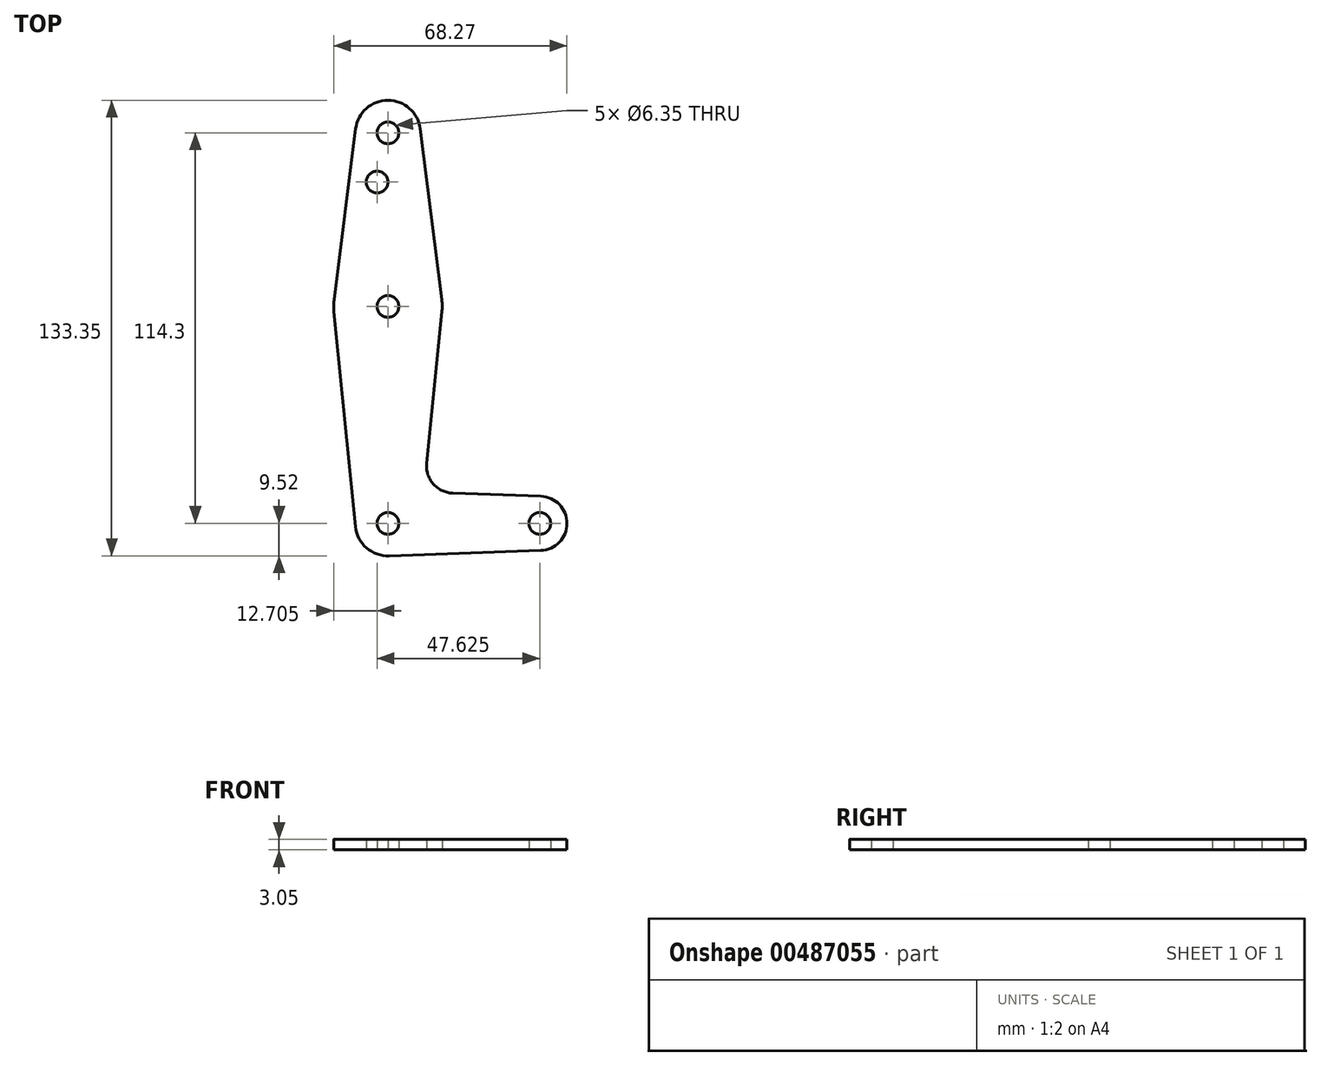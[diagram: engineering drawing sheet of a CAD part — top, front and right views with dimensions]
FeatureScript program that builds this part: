
annotation { "Feature Type Name" : "Feature", "Feature Type Description" : "" }
export const myFeature = defineFeature(function(context is Context, id is Id, definition is map)
    precondition{}
    {
        {
            var Q0;
            Q0=qCreatedBy(makeId("Top.planeOp"),FACE);
            var sketch = newSketch(context, id + "F0", { "sketchPlane" : qUnion([Q0])});
            skLineSegment(sketch, "E0", {"start": v(0, 0) * mm, "end": v(0, 114.3) * mm, "construction": true});
            skLineSegment(sketch, "E1", {"start": v(0, 0) * mm, "end": v(44.45, 0) * mm, "construction": true});
            skCircle(sketch, "E2", {"center": v(0, 0) * mm, "radius": 9.53 * mm});
            skCircle(sketch, "E3", {"center": v(0, 114.3) * mm, "radius": 9.53 * mm});
            skCircle(sketch, "E4", {"center": v(44.45, 0) * mm, "radius": 7.94 * mm});
            skCircle(sketch, "E5", {"center": v(0, 63.5) * mm, "radius": 15.88 * mm});
            skLineSegment(sketch, "E6", {"start": v(9.45, 115.5) * mm, "end": v(15.75, 65.48) * mm});
            skLineSegment(sketch, "E7", {"start": v(-15.8, 61.91) * mm, "end": v(-9.48, -0.95) * mm});
            skLineSegment(sketch, "E8", {"start": v(-9.45, 115.5) * mm, "end": v(-15.75, 65.48) * mm});
            skLineSegment(sketch, "E9", {"start": v(11.3, 17.6) * mm, "end": v(15.8, 61.9) * mm});
            skLineSegment(sketch, "E10", {"start": v(0.34, -9.52) * mm, "end": v(44.73, -7.93) * mm});
            skLineSegment(sketch, "E11", {"start": v(18.93, 8.85) * mm, "end": v(44.73, 7.93) * mm});
            skCircle(sketch, "E12", {"center": v(0, 114.3) * mm, "radius": 3.18 * mm});
            skCircle(sketch, "E13", {"center": v(-3.18, 99.89) * mm, "radius": 3.18 * mm});
            skCircle(sketch, "E14", {"center": v(0, 63.5) * mm, "radius": 3.18 * mm});
            skCircle(sketch, "E15", {"center": v(0, 0) * mm, "radius": 3.18 * mm});
            skCircle(sketch, "E16", {"center": v(44.45, 0) * mm, "radius": 3.18 * mm});
            skArc(sketch, "E17.filletArc", {"start": v(11.3, 17.6) * mm, "mid": v(13.22, 11.57) * mm, "end": v(18.93, 8.85) * mm});
            skSolve(sketch);
        }
        {
            var Q0;
            Q0=makeQuery(id+"F0.imprint","IMPRINT",FACE,{"disambiguationData":[TD([[makeQuery(id+"F0.imprint","IMPRINT",EDGE,{"derivedFrom":sQuery(id+"F0.wireOp",EDGE,"E12")}),-1.0]])]});
            var Q1;
            {var subQ1=sQuery(id+"F0.wireOp",EDGE,"E6");Q1=makeQuery(id+"F0.imprint","IMPRINT",FACE,{"disambiguationData":[TD([[makeQuery(id+"F0.imprint","IMPRINT",EDGE,{"derivedFrom":subQ1}),-1.0]])]});}
            var Q2;
            Q2=makeQuery(id+"F0.imprint","IMPRINT",FACE,{"disambiguationData":[TD([[makeQuery(id+"F0.imprint","IMPRINT",EDGE,{"derivedFrom":sQuery(id+"F0.wireOp",EDGE,"E14")}),-1.0]])]});
            var Q3;
            {var subQ0=sQuery(id+"F0.wireOp",EDGE,"E7");Q3=makeQuery(id+"F0.imprint","IMPRINT",FACE,{"disambiguationData":[TD([[makeQuery(id+"F0.imprint","IMPRINT",EDGE,{"derivedFrom":subQ0}),1.0]])]});}
            var Q4;
            Q4=makeQuery(id+"F0.imprint","IMPRINT",FACE,{"disambiguationData":[TD([[makeQuery(id+"F0.imprint","IMPRINT",EDGE,{"derivedFrom":sQuery(id+"F0.wireOp",EDGE,"E15")}),-1.0]])]});
            var Q5;
            Q5=makeQuery(id+"F0.imprint","IMPRINT",FACE,{"disambiguationData":[TD([[makeQuery(id+"F0.imprint","IMPRINT",EDGE,{"derivedFrom":sQuery(id+"F0.wireOp",EDGE,"E16")}),-1.0]])]});
            extrude(context, id + "F1", {"entities" : qUnion([Q0, Q1, Q2, Q3, Q4, Q5]), "depth" : 3.05 * mm});
        }
    });
